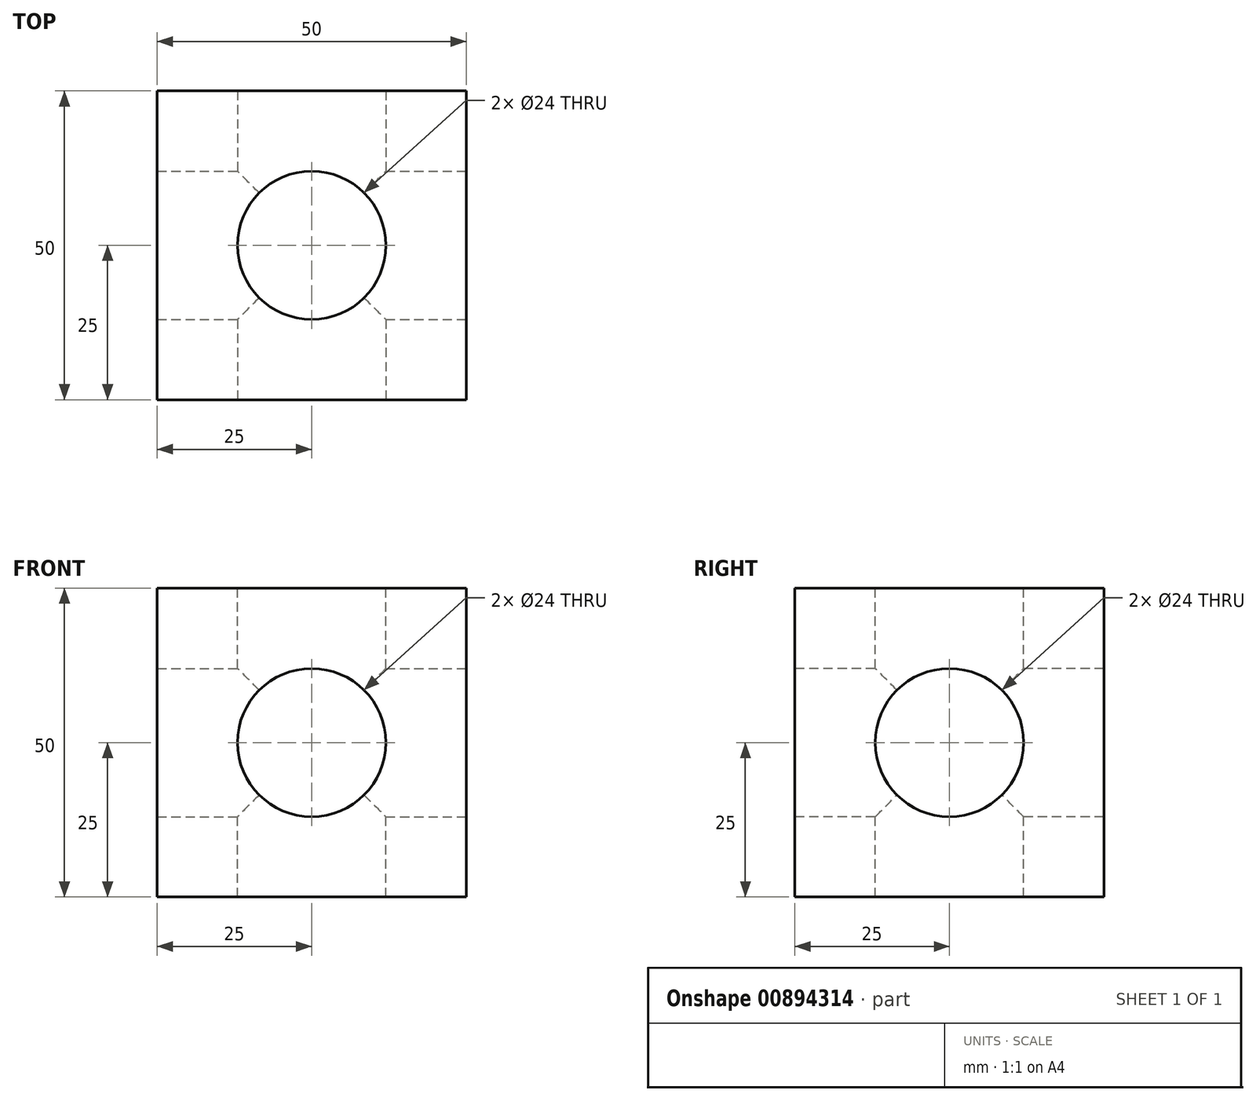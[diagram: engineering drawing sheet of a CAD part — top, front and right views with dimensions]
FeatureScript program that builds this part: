
annotation { "Feature Type Name" : "Feature", "Feature Type Description" : "" }
export const myFeature = defineFeature(function(context is Context, id is Id, definition is map)
    precondition{}
    {
        {
            var Q0;
            Q0=qCreatedBy(makeId("Front.planeOp"),FACE);
            var sketch = newSketch(context, id + "F0", { "sketchPlane" : qUnion([Q0])});
            skLineSegment(sketch, "E0.bottom", {"start": v(-25, 25) * mm, "end": v(25, 25) * mm});
            skLineSegment(sketch, "E0.top", {"start": v(-25, -25) * mm, "end": v(25, -25) * mm});
            skLineSegment(sketch, "E0.left", {"start": v(-25, 25) * mm, "end": v(-25, -25) * mm});
            skLineSegment(sketch, "E0.right", {"start": v(25, 25) * mm, "end": v(25, -25) * mm});
            skSolve(sketch);
        }
        {
            var Q0;
            Q0=makeQuery(id+"F0.imprint","IMPRINT",FACE,{"disambiguationData":[TD([[makeQuery(id+"F0.imprint","IMPRINT",EDGE,{"derivedFrom":sQuery(id+"F0.wireOp",EDGE,"E0.bottom")}),-1.0]])]});
            extrude(context, id + "F1", {"entities" : qUnion([Q0]), "depth" : 25 * mm, "offsetDistance" : 25 * mm, "hasSecondDirection" : true, "secondDirectionOppositeDirection" : true, "secondDirectionDepth" : 25 * mm});
        }
        {
            var Q0;
            Q0=makeQuery(id+"F1.opExtrude","CAP_FACE",FACE,{"disambiguationData":[OSD([sQuery(id+"F0.wireOp",EDGE,"E0.bottom"),sQuery(id+"F0.wireOp",EDGE,"E0.top"),sQuery(id+"F0.wireOp",EDGE,"E0.left"),sQuery(id+"F0.wireOp",EDGE,"E0.right")])],"isStart":false});
            var sketch = newSketch(context, id + "F2", { "sketchPlane" : qUnion([Q0])});
            skCircle(sketch, "E1", {"center": v(0, 0) * mm, "radius": 12 * mm});
            skSolve(sketch);
        }
        {
            var Q0;
            Q0=makeQuery(id+"F2.imprint","IMPRINT",FACE,{"disambiguationData":[TD([[makeQuery(id+"F2.imprint","IMPRINT",EDGE,{"derivedFrom":sQuery(id+"F2.wireOp",EDGE,"E1")}),1.0]])]});
            extrude(context, id + "F3", {"entities" : qUnion([Q0]), "operationType" : NewBodyOperationType.REMOVE, "oppositeDirection" : true, "depth" : 50 * mm, "offsetDistance" : 25 * mm});
        }
        {
            var Q0;
            Q0=makeQuery(id+"F1.opExtrude","SWEPT_FACE",FACE,{"disambiguationData":[OSD([sQuery(id+"F0.wireOp",EDGE,"E0.bottom")])]});
            var sketch = newSketch(context, id + "F4", { "sketchPlane" : qUnion([Q0])});
            skCircle(sketch, "E2", {"center": v(0, 0) * mm, "radius": 12 * mm});
            skSolve(sketch);
        }
        {
            var Q0;
            Q0=makeQuery(id+"F4.imprint","IMPRINT",FACE,{"disambiguationData":[TD([[makeQuery(id+"F4.imprint","IMPRINT",EDGE,{"derivedFrom":sQuery(id+"F4.wireOp",EDGE,"E2")}),1.0]])]});
            extrude(context, id + "F5", {"entities" : qUnion([Q0]), "operationType" : NewBodyOperationType.REMOVE, "oppositeDirection" : true, "depth" : 50 * mm, "offsetDistance" : 25 * mm});
        }
        {
            var Q0;
            Q0=makeQuery(id+"F1.opExtrude","SWEPT_FACE",FACE,{"disambiguationData":[OSD([sQuery(id+"F0.wireOp",EDGE,"E0.right")])]});
            var sketch = newSketch(context, id + "F6", { "sketchPlane" : qUnion([Q0])});
            skCircle(sketch, "E3", {"center": v(0, 0) * mm, "radius": 12 * mm});
            skSolve(sketch);
        }
        {
            var Q0;
            Q0=makeQuery(id+"F6.imprint","IMPRINT",FACE,{"disambiguationData":[TD([[makeQuery(id+"F6.imprint","IMPRINT",EDGE,{"derivedFrom":sQuery(id+"F6.wireOp",EDGE,"E3")}),1.0]])]});
            extrude(context, id + "F7", {"entities" : qUnion([Q0]), "operationType" : NewBodyOperationType.REMOVE, "oppositeDirection" : true, "depth" : 50 * mm, "offsetDistance" : 25 * mm});
        }
    });
